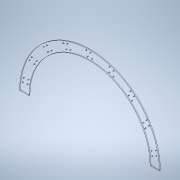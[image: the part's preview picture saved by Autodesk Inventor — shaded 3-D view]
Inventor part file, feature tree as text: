
AUTODESK INVENTOR PART (.ipt)
format: ipt  version: 2020.3 (Build 243373000, 373)  size: 177,152 bytes
history: native  units: mm
features: extrude x3, sketch x3, pattern_circular x1
ambient origin geometry x8: Origin, YZ Plane, XZ Plane, XY Plane, X Axis, Y Axis, Z Axis, Center Point
bodies: Solid1 (feature_tree)
feature tree (7):
  extrude  "Extrusion1"  Depth=40.0mm
  extrude  "Extrusion2"  Depth=10.0mm TaperAngle=0.0deg
  extrude  "Extrusion3"  Depth=3.0mm
  pattern_circular  "Circular Pattern1"  Count=27  [1 undecoded]
  sketch  "Sketch1"  dims[d0=600.0mm d1=40.0mm]
  sketch  "Sketch2"  dims[d2=4.0mm d3=0.0mm d4=10.0mm d5=0.0mm]
  sketch  "Sketch3"  dims[d6=3.0mm d7=3.0mm d9=270.0mm d11=3.0mm d12=3.0mm d14=270.0mm d16=0.0mm d17=0.0mm d18=90.0mm d19=27.925268mm d21=19.024089mm d22=20.0mm d23=1.396263mm d24=2.094395mm]
note: 1 required parameter value undecoded (feature->parameter linkage not recoverable at this tier; creation-order binding heuristic only, values carry confidence <= 0.55)
